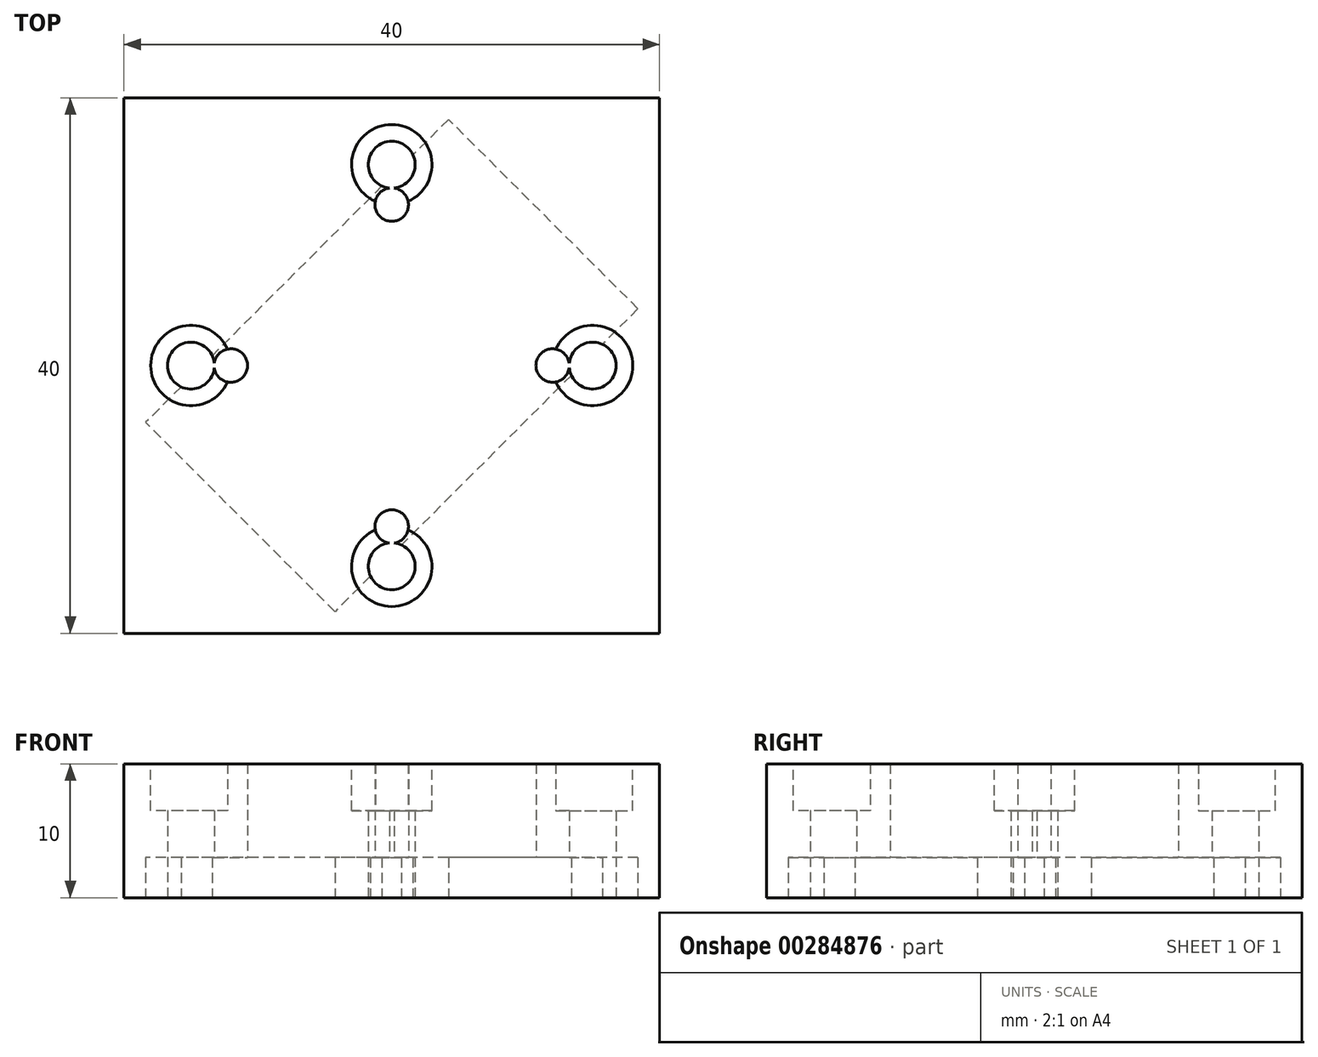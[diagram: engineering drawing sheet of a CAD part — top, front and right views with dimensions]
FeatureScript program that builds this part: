
annotation { "Feature Type Name" : "Feature", "Feature Type Description" : "" }
export const myFeature = defineFeature(function(context is Context, id is Id, definition is map)
    precondition{}
    {
        {
            var Q0;
            Q0=qCreatedBy(makeId("Top.planeOp"),FACE);
            var sketch = newSketch(context, id + "F0", { "sketchPlane" : qUnion([Q0])});
            skLineSegment(sketch, "E0.bottom", {"start": v(-20, 20) * mm, "end": v(20, 20) * mm});
            skLineSegment(sketch, "E0.top", {"start": v(-20, -20) * mm, "end": v(20, -20) * mm});
            skLineSegment(sketch, "E0.left", {"start": v(-20, 20) * mm, "end": v(-20, -20) * mm});
            skLineSegment(sketch, "E0.right", {"start": v(20, 20) * mm, "end": v(20, -20) * mm});
            skCircle(sketch, "E1", {"center": v(0, 15) * mm, "radius": 1.75 * mm});
            skCircle(sketch, "E2", {"center": v(-15, 0) * mm, "radius": 1.75 * mm});
            skCircle(sketch, "E3", {"center": v(15, 0) * mm, "radius": 1.75 * mm});
            skCircle(sketch, "E4", {"center": v(0, -15) * mm, "radius": 1.75 * mm});
            skSolve(sketch);
        }
        {
            var Q0;
            Q0 = qSketchRegion(id + "F0", true);
            extrude(context, id + "F1", {"entities" : qUnion([Q0]), "depth" : 10 * mm});
        }
        {
            var Q0;
            Q0=makeQuery(id+"F1.opExtrude","CAP_FACE",FACE,{"disambiguationData":[OSD([sQuery(id+"F0.wireOp",EDGE,"E0.bottom"),sQuery(id+"F0.wireOp",EDGE,"E0.top"),sQuery(id+"F0.wireOp",EDGE,"E0.left"),sQuery(id+"F0.wireOp",EDGE,"E0.right"),sQuery(id+"F0.wireOp",EDGE,"E1"),sQuery(id+"F0.wireOp",EDGE,"E2"),sQuery(id+"F0.wireOp",EDGE,"E3"),sQuery(id+"F0.wireOp",EDGE,"E4")])],"isStart":false});
            var sketch = newSketch(context, id + "F2", { "sketchPlane" : qUnion([Q0])});
            skCircle(sketch, "E5", {"center": v(-15, 0) * mm, "radius": 3 * mm});
            skCircle(sketch, "E6", {"center": v(0, 15) * mm, "radius": 3 * mm});
            skCircle(sketch, "E7", {"center": v(15, 0) * mm, "radius": 3 * mm});
            skCircle(sketch, "E8", {"center": v(0, -15) * mm, "radius": 3 * mm});
            skSolve(sketch);
        }
        {
            var Q0;
            Q0 = qSketchRegion(id + "F2", true);
            extrude(context, id + "F3", {"entities" : qUnion([Q0]), "operationType" : NewBodyOperationType.REMOVE, "oppositeDirection" : true, "depth" : 3.5 * mm});
        }
        {
            var Q0;
            Q0=makeQuery(id+"F1.opExtrude","CAP_FACE",FACE,{"disambiguationData":[OSD([sQuery(id+"F0.wireOp",EDGE,"E0.bottom"),sQuery(id+"F0.wireOp",EDGE,"E0.top"),sQuery(id+"F0.wireOp",EDGE,"E0.left"),sQuery(id+"F0.wireOp",EDGE,"E0.right"),sQuery(id+"F0.wireOp",EDGE,"E1"),sQuery(id+"F0.wireOp",EDGE,"E2"),sQuery(id+"F0.wireOp",EDGE,"E3"),sQuery(id+"F0.wireOp",EDGE,"E4")])],"isStart":true});
            var sketch = newSketch(context, id + "F4", { "sketchPlane" : qUnion([Q0])});
            skLineSegment(sketch, "E9", {"start": v(-20, -20) * mm, "end": v(20, 20) * mm, "construction": true});
            skLineSegment(sketch, "E10.bottom", {"start": v(18.38, -4.24) * mm, "end": v(4.24, -18.38) * mm});
            skLineSegment(sketch, "E10.top", {"start": v(-4.24, 18.38) * mm, "end": v(-18.38, 4.24) * mm});
            skLineSegment(sketch, "E10.left", {"start": v(4.24, -18.38) * mm, "end": v(-18.38, 4.24) * mm});
            skLineSegment(sketch, "E10.right", {"start": v(18.38, -4.24) * mm, "end": v(-4.24, 18.38) * mm});
            skPoint(sketch, "E10.middle", {"position": v(0, 0) * mm});
            skLineSegment(sketch, "E11", {"start": v(-20, 20) * mm, "end": v(20, -20) * mm, "construction": true});
            skSolve(sketch);
        }
        {
            var Q0;
            Q0 = qSketchRegion(id + "F4", true);
            extrude(context, id + "F5", {"entities" : qUnion([Q0]), "operationType" : NewBodyOperationType.REMOVE, "oppositeDirection" : true, "depth" : 3 * mm});
        }
        {
            var Q0;
            Q0=makeQuery(id+"F1.opExtrude","CAP_FACE",FACE,{"disambiguationData":[OSD([sQuery(id+"F0.wireOp",EDGE,"E0.bottom"),sQuery(id+"F0.wireOp",EDGE,"E0.top"),sQuery(id+"F0.wireOp",EDGE,"E0.left"),sQuery(id+"F0.wireOp",EDGE,"E0.right"),sQuery(id+"F0.wireOp",EDGE,"E1"),sQuery(id+"F0.wireOp",EDGE,"E2"),sQuery(id+"F0.wireOp",EDGE,"E3"),sQuery(id+"F0.wireOp",EDGE,"E4")])],"isStart":true});
            var sketch = newSketch(context, id + "F6", { "sketchPlane" : qUnion([Q0])});
            skLineSegment(sketch, "E12", {"start": v(-20, 20) * mm, "end": v(20, -20) * mm, "construction": true});
            skLineSegment(sketch, "E13", {"start": v(-20, -20) * mm, "end": v(20, 20) * mm, "construction": true});
            skCircle(sketch, "E14", {"center": v(0, 12.02) * mm, "radius": 1.25 * mm});
            skCircle(sketch, "E15", {"center": v(12.02, 0) * mm, "radius": 1.25 * mm});
            skCircle(sketch, "E16", {"center": v(-12.02, 0) * mm, "radius": 1.25 * mm});
            skCircle(sketch, "E17", {"center": v(0, -12.02) * mm, "radius": 1.25 * mm});
            skSolve(sketch);
        }
        {
            var Q0;
            Q0 = qSketchRegion(id + "F6", true);
            extrude(context, id + "F7", {"entities" : qUnion([Q0]), "operationType" : NewBodyOperationType.REMOVE, "endBound" : BoundingType.THROUGH_ALL, "oppositeDirection" : true, "depth" : 25 * mm});
        }
    });
